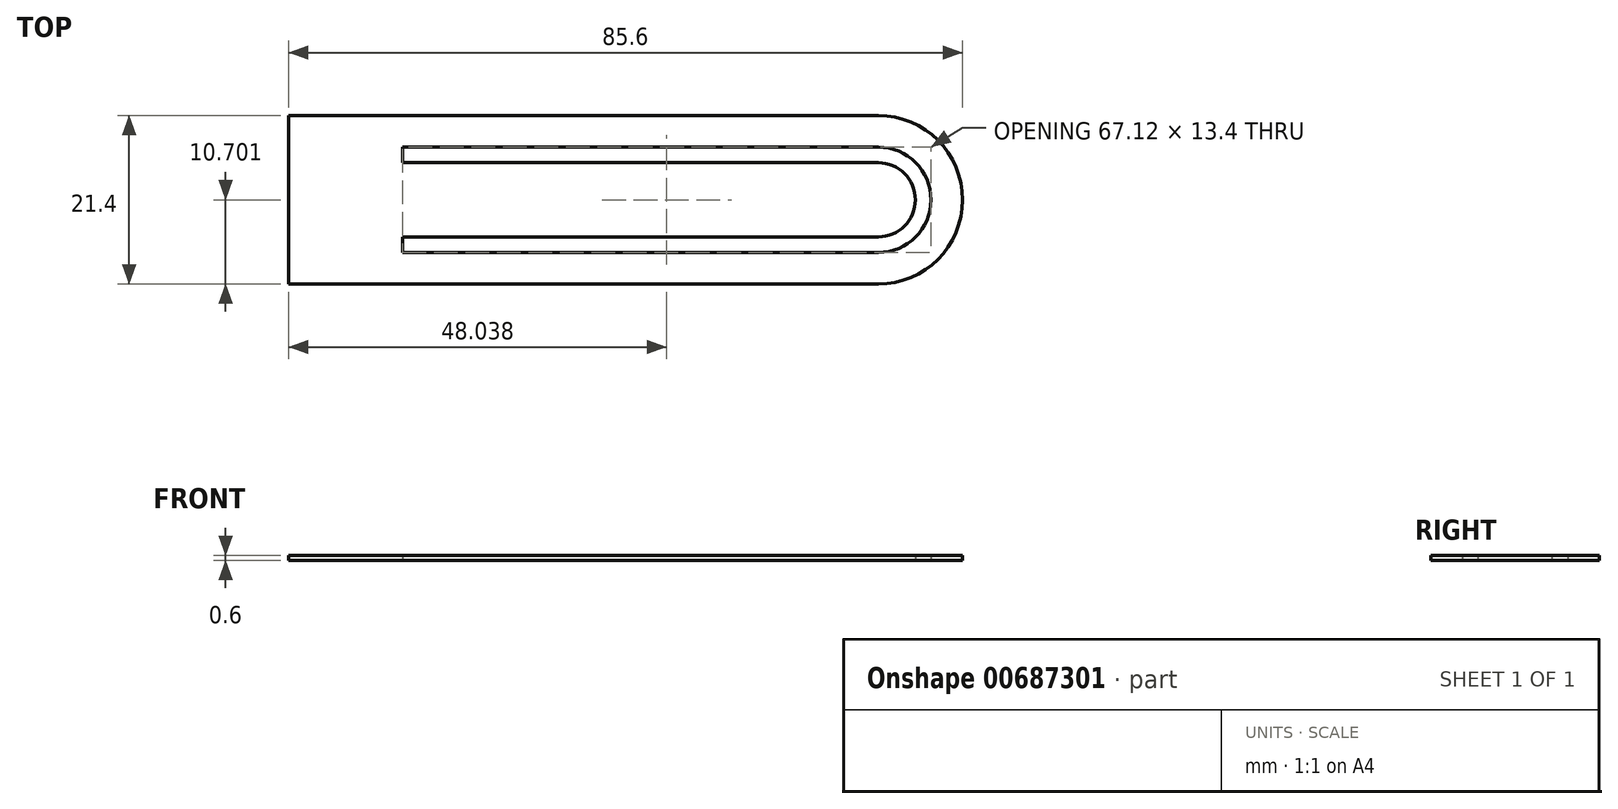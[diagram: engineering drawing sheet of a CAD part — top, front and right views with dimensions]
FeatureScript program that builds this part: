
annotation { "Feature Type Name" : "Feature", "Feature Type Description" : "" }
export const myFeature = defineFeature(function(context is Context, id is Id, definition is map)
    precondition{}
    {
        {
            var Q0;
            Q0=qCreatedBy(makeId("Top.planeOp"),FACE);
            var sketch = newSketch(context, id + "F0", { "sketchPlane" : qUnion([Q0])});
            skLineSegment(sketch, "E0.bottom", {"start": v(32.1, -13.46) * mm, "end": v(-42.8, -13.46) * mm});
            skLineSegment(sketch, "E0.top", {"start": v(32.1, 7.94) * mm, "end": v(-42.8, 7.94) * mm});
            skLineSegment(sketch, "E0.left", {"start": v(42.8, -2.76) * mm, "end": v(42.8, -2.76) * mm});
            skLineSegment(sketch, "E0.right", {"start": v(-42.8, -13.46) * mm, "end": v(-42.8, 7.94) * mm});
            skPoint(sketch, "E0.middle", {"position": v(0, -2.76) * mm});
            skPoint(sketch, "E1.visualSharp", {"position": v(42.8, 7.94) * mm});
            skArc(sketch, "E1.filletArc", {"start": v(42.8, -2.76) * mm, "mid": v(39.67, 4.8) * mm, "end": v(32.1, 7.94) * mm});
            skPoint(sketch, "E2.visualSharp", {"position": v(42.8, -13.46) * mm});
            skArc(sketch, "E2.filletArc", {"start": v(32.1, -13.46) * mm, "mid": v(39.67, -10.32) * mm, "end": v(42.8, -2.76) * mm});
            skLineSegment(sketch, "E3.1", {"start": v(32.1, 3.94) * mm, "end": v(-28.32, 3.94) * mm});
            skLineSegment(sketch, "E3.2", {"start": v(32.1, -9.46) * mm, "end": v(-28.32, -9.46) * mm});
            skArc(sketch, "E3.3", {"start": v(32.1, -9.46) * mm, "mid": v(36.84, -7.5) * mm, "end": v(38.8, -2.76) * mm});
            skArc(sketch, "E3.4", {"start": v(38.8, -2.76) * mm, "mid": v(36.84, 1.98) * mm, "end": v(32.1, 3.94) * mm});
            skLineSegment(sketch, "E4.0", {"start": v(32, 1.94) * mm, "end": v(-28.32, 1.94) * mm});
            skText(sketch, "E5", { "text": "LIBERTO", "fontName": "AllertaStencil-Regular.ttf"});
            skLineSegment(sketch, "E6.0", {"start": v(32.1, -7.46) * mm, "end": v(-28.32, -7.46) * mm});
            skArc(sketch, "E7.0", {"start": v(36.8, -2.76) * mm, "mid": v(35.42, 0.56) * mm, "end": v(32.1, 1.94) * mm});
            skArc(sketch, "E7.1", {"start": v(32.1, -7.46) * mm, "mid": v(35.42, -6.08) * mm, "end": v(36.8, -2.76) * mm});
            skLineSegment(sketch, "E8", {"start": v(-28.32, 3.94) * mm, "end": v(-28.32, 1.94) * mm});
            skLineSegment(sketch, "E9.trimOffspring", {"start": v(-28.32, -7.46) * mm, "end": v(-28.32, -9.46) * mm});
            skLineSegment(sketch, "E10", {"start": v(32, 1.94) * mm, "end": v(32.1, 1.94) * mm});
            const initialGuessF0  = {"E5": [-0.03845, -0.01246, 0, 1, 0.00335]};
            skSetInitialGuess(sketch, initialGuessF0);
            skSolve(sketch);
        }
        {
            var Q0;
            Q0=qCreatedBy(makeId("Top.planeOp"),FACE);
            var sketch = newSketch(context, id + "F1", { "sketchPlane" : qUnion([Q0])});
            skLineSegment(sketch, "E11.bottom", {"start": v(-36.45, -3.76) * mm, "end": v(-34.45, -3.76) * mm});
            skLineSegment(sketch, "E11.top", {"start": v(-36.45, -5.76) * mm, "end": v(-34.45, -5.76) * mm});
            skLineSegment(sketch, "E11.left", {"start": v(-36.45, -3.76) * mm, "end": v(-36.45, -5.76) * mm});
            skLineSegment(sketch, "E11.right", {"start": v(-34.45, -3.76) * mm, "end": v(-34.45, -5.76) * mm});
            skLineSegment(sketch, "E12.bottom", {"start": v(-36.45, 0.24) * mm, "end": v(-34.45, 0.24) * mm});
            skLineSegment(sketch, "E12.top", {"start": v(-36.45, -1.76) * mm, "end": v(-34.45, -1.76) * mm});
            skLineSegment(sketch, "E12.left", {"start": v(-36.45, 0.24) * mm, "end": v(-36.45, -1.76) * mm});
            skLineSegment(sketch, "E12.right", {"start": v(-34.45, 0.24) * mm, "end": v(-34.45, -1.76) * mm});
            skLineSegment(sketch, "E13", {"start": v(-34.45, -1.76) * mm, "end": v(-34.45, -3.76) * mm});
            skLineSegment(sketch, "E14", {"start": v(-34.45, -1.76) * mm, "end": v(-33.45, -1.76) * mm});
            skLineSegment(sketch, "E15", {"start": v(-33.45, -1.76) * mm, "end": v(-33.45, -0.76) * mm});
            skLineSegment(sketch, "E16", {"start": v(-33.45, -0.76) * mm, "end": v(-30.45, -0.76) * mm});
            skLineSegment(sketch, "E17", {"start": v(-30.45, -0.76) * mm, "end": v(-30.45, -1.76) * mm});
            skLineSegment(sketch, "E18", {"start": v(-30.45, -1.76) * mm, "end": v(-31.45, -1.76) * mm});
            skLineSegment(sketch, "E19", {"start": v(-31.45, -1.76) * mm, "end": v(-31.45, -3.76) * mm});
            skLineSegment(sketch, "E20", {"start": v(-31.45, -3.76) * mm, "end": v(-30.45, -3.76) * mm});
            skLineSegment(sketch, "E21", {"start": v(-30.45, -3.76) * mm, "end": v(-30.45, -4.76) * mm});
            skLineSegment(sketch, "E22", {"start": v(-30.45, -4.76) * mm, "end": v(-33.45, -4.76) * mm});
            skLineSegment(sketch, "E23", {"start": v(-33.45, -4.76) * mm, "end": v(-33.45, -3.76) * mm});
            skLineSegment(sketch, "E24", {"start": v(-33.45, -3.76) * mm, "end": v(-34.45, -3.76) * mm});
            skLineSegment(sketch, "E25", {"start": v(-34.41, -3.76) * mm, "end": v(-34.41, -1.76) * mm});
            skSolve(sketch);
        }
        {
            var Q0;
            Q0=makeQuery(id+"F1.imprint","IMPRINT",FACE,{"disambiguationData":[TD([[makeQuery(id+"F1.imprint","IMPRINT",EDGE,{"derivedFrom":sQuery(id+"F1.wireOp",EDGE,"E12.bottom")}),-1.0]])]});
            var Q1;
            Q1=makeQuery(id+"F1.imprint","IMPRINT",FACE,{"disambiguationData":[TD([[makeQuery(id+"F1.imprint","IMPRINT",EDGE,{"derivedFrom":sQuery(id+"F1.wireOp",EDGE,"E11.bottom")}),-1.0]])]});
            extrude(context, id + "F2", {"entities" : qUnion([Q0, Q1]), "depth" : .6 * mm, "offsetDistance" : 25 * mm});
        }
        {
            var Q0;
            Q0=makeQuery(id+"F0.imprint","IMPRINT",FACE,{"disambiguationData":[TD([[makeQuery(id+"F0.imprint","IMPRINT",EDGE,{"derivedFrom":sQuery(id+"F0.wireOp",EDGE,"E0.bottom")}),-1.0]])]});
            extrude(context, id + "F3", {"entities" : qUnion([Q0]), "depth" : .6 * mm, "offsetDistance" : 25 * mm});
        }
        {
            var Q0;
            Q0=makeQuery(id+"F2.opExtrude","SWEPT_BODY",BODY,{"disambiguationData":[OSD([sQuery(id+"F1.wireOp",EDGE,"E11.bottom"),sQuery(id+"F1.wireOp",EDGE,"E11.top"),sQuery(id+"F1.wireOp",EDGE,"E11.left"),sQuery(id+"F1.wireOp",EDGE,"E11.right")])]});
            var Q1;
            Q1=makeQuery(id+"F3.opExtrude","SWEPT_BODY",BODY,{"disambiguationData":[OSD([sQuery(id+"F0.wireOp",EDGE,"E0.bottom"),sQuery(id+"F0.wireOp",EDGE,"E0.top"),sQuery(id+"F0.wireOp",EDGE,"E0.right"),sQuery(id+"F0.wireOp",EDGE,"E1.filletArc"),sQuery(id+"F0.wireOp",EDGE,"E2.filletArc"),sQuery(id+"F0.wireOp",EDGE,"E3.1"),sQuery(id+"F0.wireOp",EDGE,"E3.2"),sQuery(id+"F0.wireOp",EDGE,"E3.3"),sQuery(id+"F0.wireOp",EDGE,"E3.4"),sQuery(id+"F0.wireOp",EDGE,"E4.0"),sQuery(id+"F0.wireOp",EDGE,"E5.sketch_text.stroke-0"),sQuery(id+"F0.wireOp",EDGE,"E5.sketch_text.stroke-1"),sQuery(id+"F0.wireOp",EDGE,"E5.sketch_text.stroke-2"),sQuery(id+"F0.wireOp",EDGE,"E5.sketch_text.stroke-3"),sQuery(id+"F0.wireOp",EDGE,"E5.sketch_text.stroke-4"),sQuery(id+"F0.wireOp",EDGE,"E5.sketch_text.stroke-5"),sQuery(id+"F0.wireOp",EDGE,"E5.sketch_text.stroke-6"),sQuery(id+"F0.wireOp",EDGE,"E5.sketch_text.stroke-7"),sQuery(id+"F0.wireOp",EDGE,"E5.sketch_text.stroke-8"),sQuery(id+"F0.wireOp",EDGE,"E5.sketch_text.stroke-9"),sQuery(id+"F0.wireOp",EDGE,"E5.sketch_text.stroke-10"),sQuery(id+"F0.wireOp",EDGE,"E5.sketch_text.stroke-11"),sQuery(id+"F0.wireOp",EDGE,"E5.sketch_text.stroke-12"),sQuery(id+"F0.wireOp",EDGE,"E5.sketch_text.stroke-13"),sQuery(id+"F0.wireOp",EDGE,"E5.sketch_text.stroke-14"),sQuery(id+"F0.wireOp",EDGE,"E5.sketch_text.stroke-15"),sQuery(id+"F0.wireOp",EDGE,"E5.sketch_text.stroke-16"),sQuery(id+"F0.wireOp",EDGE,"E5.sketch_text.stroke-17"),sQuery(id+"F0.wireOp",EDGE,"E5.sketch_text.stroke-18"),sQuery(id+"F0.wireOp",EDGE,"E5.sketch_text.stroke-19"),sQuery(id+"F0.wireOp",EDGE,"E5.sketch_text.stroke-20"),sQuery(id+"F0.wireOp",EDGE,"E5.sketch_text.stroke-21"),sQuery(id+"F0.wireOp",EDGE,"E5.sketch_text.stroke-22"),sQuery(id+"F0.wireOp",EDGE,"E5.sketch_text.stroke-23"),sQuery(id+"F0.wireOp",EDGE,"E5.sketch_text.stroke-24"),sQuery(id+"F0.wireOp",EDGE,"E5.sketch_text.stroke-25"),sQuery(id+"F0.wireOp",EDGE,"E5.sketch_text.stroke-26"),sQuery(id+"F0.wireOp",EDGE,"E5.sketch_text.stroke-27"),sQuery(id+"F0.wireOp",EDGE,"E5.sketch_text.stroke-28"),sQuery(id+"F0.wireOp",EDGE,"E5.sketch_text.stroke-29"),sQuery(id+"F0.wireOp",EDGE,"E5.sketch_text.stroke-30"),sQuery(id+"F0.wireOp",EDGE,"E5.sketch_text.stroke-31"),sQuery(id+"F0.wireOp",EDGE,"E5.sketch_text.stroke-32"),sQuery(id+"F0.wireOp",EDGE,"E5.sketch_text.stroke-33"),sQuery(id+"F0.wireOp",EDGE,"E5.sketch_text.stroke-34"),sQuery(id+"F0.wireOp",EDGE,"E5.sketch_text.stroke-35"),sQuery(id+"F0.wireOp",EDGE,"E5.sketch_text.stroke-36"),sQuery(id+"F0.wireOp",EDGE,"E5.sketch_text.stroke-37"),sQuery(id+"F0.wireOp",EDGE,"E5.sketch_text.stroke-38"),sQuery(id+"F0.wireOp",EDGE,"E5.sketch_text.stroke-39"),sQuery(id+"F0.wireOp",EDGE,"E5.sketch_text.stroke-40"),sQuery(id+"F0.wireOp",EDGE,"E5.sketch_text.stroke-41"),sQuery(id+"F0.wireOp",EDGE,"E5.sketch_text.stroke-42"),sQuery(id+"F0.wireOp",EDGE,"E5.sketch_text.stroke-43"),sQuery(id+"F0.wireOp",EDGE,"E5.sketch_text.stroke-44"),sQuery(id+"F0.wireOp",EDGE,"E5.sketch_text.stroke-45"),sQuery(id+"F0.wireOp",EDGE,"E5.sketch_text.stroke-46"),sQuery(id+"F0.wireOp",EDGE,"E5.sketch_text.stroke-47"),sQuery(id+"F0.wireOp",EDGE,"E5.sketch_text.stroke-48"),sQuery(id+"F0.wireOp",EDGE,"E5.sketch_text.stroke-49"),sQuery(id+"F0.wireOp",EDGE,"E5.sketch_text.stroke-50"),sQuery(id+"F0.wireOp",EDGE,"E5.sketch_text.stroke-51"),sQuery(id+"F0.wireOp",EDGE,"E5.sketch_text.stroke-52"),sQuery(id+"F0.wireOp",EDGE,"E5.sketch_text.stroke-53"),sQuery(id+"F0.wireOp",EDGE,"E5.sketch_text.stroke-54"),sQuery(id+"F0.wireOp",EDGE,"E5.sketch_text.stroke-55"),sQuery(id+"F0.wireOp",EDGE,"E5.sketch_text.stroke-56"),sQuery(id+"F0.wireOp",EDGE,"E5.sketch_text.stroke-57"),sQuery(id+"F0.wireOp",EDGE,"E5.sketch_text.stroke-58"),sQuery(id+"F0.wireOp",EDGE,"E5.sketch_text.stroke-59"),sQuery(id+"F0.wireOp",EDGE,"E5.sketch_text.stroke-60"),sQuery(id+"F0.wireOp",EDGE,"E5.sketch_text.stroke-61"),sQuery(id+"F0.wireOp",EDGE,"E5.sketch_text.stroke-62"),sQuery(id+"F0.wireOp",EDGE,"E5.sketch_text.stroke-63"),sQuery(id+"F0.wireOp",EDGE,"E5.sketch_text.stroke-64"),sQuery(id+"F0.wireOp",EDGE,"E5.sketch_text.stroke-65"),sQuery(id+"F0.wireOp",EDGE,"E5.sketch_text.stroke-66"),sQuery(id+"F0.wireOp",EDGE,"E5.sketch_text.stroke-67"),sQuery(id+"F0.wireOp",EDGE,"E5.sketch_text.stroke-68"),sQuery(id+"F0.wireOp",EDGE,"E5.sketch_text.stroke-69"),sQuery(id+"F0.wireOp",EDGE,"E5.sketch_text.stroke-70"),sQuery(id+"F0.wireOp",EDGE,"E5.sketch_text.stroke-71"),sQuery(id+"F0.wireOp",EDGE,"E5.sketch_text.stroke-72"),sQuery(id+"F0.wireOp",EDGE,"E5.sketch_text.stroke-73"),sQuery(id+"F0.wireOp",EDGE,"E5.sketch_text.stroke-74"),sQuery(id+"F0.wireOp",EDGE,"E5.sketch_text.stroke-75"),sQuery(id+"F0.wireOp",EDGE,"E5.sketch_text.stroke-76"),sQuery(id+"F0.wireOp",EDGE,"E5.sketch_text.stroke-77"),sQuery(id+"F0.wireOp",EDGE,"E5.sketch_text.stroke-78"),sQuery(id+"F0.wireOp",EDGE,"E5.sketch_text.stroke-79"),sQuery(id+"F0.wireOp",EDGE,"E5.sketch_text.stroke-80"),sQuery(id+"F0.wireOp",EDGE,"E5.sketch_text.stroke-81"),sQuery(id+"F0.wireOp",EDGE,"E5.sketch_text.stroke-82"),sQuery(id+"F0.wireOp",EDGE,"E5.sketch_text.stroke-83"),sQuery(id+"F0.wireOp",EDGE,"E5.sketch_text.stroke-84"),sQuery(id+"F0.wireOp",EDGE,"E5.sketch_text.stroke-85"),sQuery(id+"F0.wireOp",EDGE,"E5.sketch_text.stroke-86"),sQuery(id+"F0.wireOp",EDGE,"E5.sketch_text.stroke-87"),sQuery(id+"F0.wireOp",EDGE,"E5.sketch_text.stroke-88"),sQuery(id+"F0.wireOp",EDGE,"E5.sketch_text.stroke-89"),sQuery(id+"F0.wireOp",EDGE,"E5.sketch_text.stroke-90"),sQuery(id+"F0.wireOp",EDGE,"E5.sketch_text.stroke-91"),sQuery(id+"F0.wireOp",EDGE,"E5.sketch_text.stroke-92"),sQuery(id+"F0.wireOp",EDGE,"E5.sketch_text.stroke-93"),sQuery(id+"F0.wireOp",EDGE,"E5.sketch_text.stroke-94"),sQuery(id+"F0.wireOp",EDGE,"E5.sketch_text.stroke-95"),sQuery(id+"F0.wireOp",EDGE,"E5.sketch_text.stroke-96"),sQuery(id+"F0.wireOp",EDGE,"E5.sketch_text.stroke-97"),sQuery(id+"F0.wireOp",EDGE,"E5.sketch_text.stroke-98"),sQuery(id+"F0.wireOp",EDGE,"E5.sketch_text.stroke-99"),sQuery(id+"F0.wireOp",EDGE,"E5.sketch_text.stroke-100"),sQuery(id+"F0.wireOp",EDGE,"E5.sketch_text.stroke-101"),sQuery(id+"F0.wireOp",EDGE,"E5.sketch_text.stroke-102"),sQuery(id+"F0.wireOp",EDGE,"E5.sketch_text.stroke-103"),sQuery(id+"F0.wireOp",EDGE,"E5.sketch_text.stroke-104"),sQuery(id+"F0.wireOp",EDGE,"E5.sketch_text.stroke-105"),sQuery(id+"F0.wireOp",EDGE,"E5.sketch_text.stroke-106"),sQuery(id+"F0.wireOp",EDGE,"E5.sketch_text.stroke-107"),sQuery(id+"F0.wireOp",EDGE,"E5.sketch_text.stroke-108"),sQuery(id+"F0.wireOp",EDGE,"E5.sketch_text.stroke-109"),sQuery(id+"F0.wireOp",EDGE,"E5.sketch_text.stroke-110"),sQuery(id+"F0.wireOp",EDGE,"E5.sketch_text.stroke-111"),sQuery(id+"F0.wireOp",EDGE,"E5.sketch_text.stroke-112"),sQuery(id+"F0.wireOp",EDGE,"E5.sketch_text.stroke-113"),sQuery(id+"F0.wireOp",EDGE,"E5.sketch_text.stroke-114"),sQuery(id+"F0.wireOp",EDGE,"E5.sketch_text.stroke-115"),sQuery(id+"F0.wireOp",EDGE,"E5.sketch_text.stroke-116"),sQuery(id+"F0.wireOp",EDGE,"E5.sketch_text.stroke-117"),sQuery(id+"F0.wireOp",EDGE,"E5.sketch_text.stroke-118"),sQuery(id+"F0.wireOp",EDGE,"E5.sketch_text.stroke-119"),sQuery(id+"F0.wireOp",EDGE,"E5.sketch_text.stroke-120"),sQuery(id+"F0.wireOp",EDGE,"E5.sketch_text.stroke-121"),sQuery(id+"F0.wireOp",EDGE,"E5.sketch_text.stroke-122"),sQuery(id+"F0.wireOp",EDGE,"E5.sketch_text.stroke-123"),sQuery(id+"F0.wireOp",EDGE,"E5.sketch_text.stroke-124"),sQuery(id+"F0.wireOp",EDGE,"E5.sketch_text.stroke-125"),sQuery(id+"F0.wireOp",EDGE,"E5.sketch_text.stroke-126"),sQuery(id+"F0.wireOp",EDGE,"E5.sketch_text.stroke-127"),sQuery(id+"F0.wireOp",EDGE,"E5.sketch_text.stroke-128"),sQuery(id+"F0.wireOp",EDGE,"E5.sketch_text.stroke-129"),sQuery(id+"F0.wireOp",EDGE,"E5.sketch_text.stroke-130"),sQuery(id+"F0.wireOp",EDGE,"E5.sketch_text.stroke-131"),sQuery(id+"F0.wireOp",EDGE,"E5.sketch_text.stroke-132"),sQuery(id+"F0.wireOp",EDGE,"E5.sketch_text.stroke-133"),sQuery(id+"F0.wireOp",EDGE,"E5.sketch_text.stroke-134"),sQuery(id+"F0.wireOp",EDGE,"E5.sketch_text.stroke-135"),sQuery(id+"F0.wireOp",EDGE,"E5.sketch_text.stroke-136"),sQuery(id+"F0.wireOp",EDGE,"E5.sketch_text.stroke-137"),sQuery(id+"F0.wireOp",EDGE,"E5.sketch_text.stroke-138"),sQuery(id+"F0.wireOp",EDGE,"E5.sketch_text.stroke-139"),sQuery(id+"F0.wireOp",EDGE,"E5.sketch_text.stroke-140"),sQuery(id+"F0.wireOp",EDGE,"E5.sketch_text.stroke-141"),sQuery(id+"F0.wireOp",EDGE,"E5.sketch_text.stroke-142"),sQuery(id+"F0.wireOp",EDGE,"E6.0"),sQuery(id+"F0.wireOp",EDGE,"E7.0"),sQuery(id+"F0.wireOp",EDGE,"E7.1"),sQuery(id+"F0.wireOp",EDGE,"E8"),sQuery(id+"F0.wireOp",EDGE,"E9.trimOffspring"),sQuery(id+"F0.wireOp",EDGE,"E10")])]});
            booleanBodies(context, id + "F4", {"operationType" : BooleanOperationType.SUBTRACTION, "tools" : qUnion([Q0]), "targets" : qUnion([Q1])});
        }
        {
            var Q0;
            Q0=makeQuery(id+"F2.opExtrude","SWEPT_BODY",BODY,{"disambiguationData":[OSD([sQuery(id+"F1.wireOp",EDGE,"E12.bottom"),sQuery(id+"F1.wireOp",EDGE,"E12.top"),sQuery(id+"F1.wireOp",EDGE,"E12.left"),sQuery(id+"F1.wireOp",EDGE,"E12.right")])]});
            var Q1;
            Q1=makeQuery(id+"F3.opExtrude","SWEPT_BODY",BODY,{"disambiguationData":[OSD([sQuery(id+"F0.wireOp",EDGE,"E0.bottom"),sQuery(id+"F0.wireOp",EDGE,"E0.top"),sQuery(id+"F0.wireOp",EDGE,"E0.right"),sQuery(id+"F0.wireOp",EDGE,"E1.filletArc"),sQuery(id+"F0.wireOp",EDGE,"E2.filletArc"),sQuery(id+"F0.wireOp",EDGE,"E3.1"),sQuery(id+"F0.wireOp",EDGE,"E3.2"),sQuery(id+"F0.wireOp",EDGE,"E3.3"),sQuery(id+"F0.wireOp",EDGE,"E3.4"),sQuery(id+"F0.wireOp",EDGE,"E4.0"),sQuery(id+"F0.wireOp",EDGE,"E5.sketch_text.stroke-0"),sQuery(id+"F0.wireOp",EDGE,"E5.sketch_text.stroke-1"),sQuery(id+"F0.wireOp",EDGE,"E5.sketch_text.stroke-2"),sQuery(id+"F0.wireOp",EDGE,"E5.sketch_text.stroke-3"),sQuery(id+"F0.wireOp",EDGE,"E5.sketch_text.stroke-4"),sQuery(id+"F0.wireOp",EDGE,"E5.sketch_text.stroke-5"),sQuery(id+"F0.wireOp",EDGE,"E5.sketch_text.stroke-6"),sQuery(id+"F0.wireOp",EDGE,"E5.sketch_text.stroke-7"),sQuery(id+"F0.wireOp",EDGE,"E5.sketch_text.stroke-8"),sQuery(id+"F0.wireOp",EDGE,"E5.sketch_text.stroke-9"),sQuery(id+"F0.wireOp",EDGE,"E5.sketch_text.stroke-10"),sQuery(id+"F0.wireOp",EDGE,"E5.sketch_text.stroke-11"),sQuery(id+"F0.wireOp",EDGE,"E5.sketch_text.stroke-12"),sQuery(id+"F0.wireOp",EDGE,"E5.sketch_text.stroke-13"),sQuery(id+"F0.wireOp",EDGE,"E5.sketch_text.stroke-14"),sQuery(id+"F0.wireOp",EDGE,"E5.sketch_text.stroke-15"),sQuery(id+"F0.wireOp",EDGE,"E5.sketch_text.stroke-16"),sQuery(id+"F0.wireOp",EDGE,"E5.sketch_text.stroke-17"),sQuery(id+"F0.wireOp",EDGE,"E5.sketch_text.stroke-18"),sQuery(id+"F0.wireOp",EDGE,"E5.sketch_text.stroke-19"),sQuery(id+"F0.wireOp",EDGE,"E5.sketch_text.stroke-20"),sQuery(id+"F0.wireOp",EDGE,"E5.sketch_text.stroke-21"),sQuery(id+"F0.wireOp",EDGE,"E5.sketch_text.stroke-22"),sQuery(id+"F0.wireOp",EDGE,"E5.sketch_text.stroke-23"),sQuery(id+"F0.wireOp",EDGE,"E5.sketch_text.stroke-24"),sQuery(id+"F0.wireOp",EDGE,"E5.sketch_text.stroke-25"),sQuery(id+"F0.wireOp",EDGE,"E5.sketch_text.stroke-26"),sQuery(id+"F0.wireOp",EDGE,"E5.sketch_text.stroke-27"),sQuery(id+"F0.wireOp",EDGE,"E5.sketch_text.stroke-28"),sQuery(id+"F0.wireOp",EDGE,"E5.sketch_text.stroke-29"),sQuery(id+"F0.wireOp",EDGE,"E5.sketch_text.stroke-30"),sQuery(id+"F0.wireOp",EDGE,"E5.sketch_text.stroke-31"),sQuery(id+"F0.wireOp",EDGE,"E5.sketch_text.stroke-32"),sQuery(id+"F0.wireOp",EDGE,"E5.sketch_text.stroke-33"),sQuery(id+"F0.wireOp",EDGE,"E5.sketch_text.stroke-34"),sQuery(id+"F0.wireOp",EDGE,"E5.sketch_text.stroke-35"),sQuery(id+"F0.wireOp",EDGE,"E5.sketch_text.stroke-36"),sQuery(id+"F0.wireOp",EDGE,"E5.sketch_text.stroke-37"),sQuery(id+"F0.wireOp",EDGE,"E5.sketch_text.stroke-38"),sQuery(id+"F0.wireOp",EDGE,"E5.sketch_text.stroke-39"),sQuery(id+"F0.wireOp",EDGE,"E5.sketch_text.stroke-40"),sQuery(id+"F0.wireOp",EDGE,"E5.sketch_text.stroke-41"),sQuery(id+"F0.wireOp",EDGE,"E5.sketch_text.stroke-42"),sQuery(id+"F0.wireOp",EDGE,"E5.sketch_text.stroke-43"),sQuery(id+"F0.wireOp",EDGE,"E5.sketch_text.stroke-44"),sQuery(id+"F0.wireOp",EDGE,"E5.sketch_text.stroke-45"),sQuery(id+"F0.wireOp",EDGE,"E5.sketch_text.stroke-46"),sQuery(id+"F0.wireOp",EDGE,"E5.sketch_text.stroke-47"),sQuery(id+"F0.wireOp",EDGE,"E5.sketch_text.stroke-48"),sQuery(id+"F0.wireOp",EDGE,"E5.sketch_text.stroke-49"),sQuery(id+"F0.wireOp",EDGE,"E5.sketch_text.stroke-50"),sQuery(id+"F0.wireOp",EDGE,"E5.sketch_text.stroke-51"),sQuery(id+"F0.wireOp",EDGE,"E5.sketch_text.stroke-52"),sQuery(id+"F0.wireOp",EDGE,"E5.sketch_text.stroke-53"),sQuery(id+"F0.wireOp",EDGE,"E5.sketch_text.stroke-54"),sQuery(id+"F0.wireOp",EDGE,"E5.sketch_text.stroke-55"),sQuery(id+"F0.wireOp",EDGE,"E5.sketch_text.stroke-56"),sQuery(id+"F0.wireOp",EDGE,"E5.sketch_text.stroke-57"),sQuery(id+"F0.wireOp",EDGE,"E5.sketch_text.stroke-58"),sQuery(id+"F0.wireOp",EDGE,"E5.sketch_text.stroke-59"),sQuery(id+"F0.wireOp",EDGE,"E5.sketch_text.stroke-60"),sQuery(id+"F0.wireOp",EDGE,"E5.sketch_text.stroke-61"),sQuery(id+"F0.wireOp",EDGE,"E5.sketch_text.stroke-62"),sQuery(id+"F0.wireOp",EDGE,"E5.sketch_text.stroke-63"),sQuery(id+"F0.wireOp",EDGE,"E5.sketch_text.stroke-64"),sQuery(id+"F0.wireOp",EDGE,"E5.sketch_text.stroke-65"),sQuery(id+"F0.wireOp",EDGE,"E5.sketch_text.stroke-66"),sQuery(id+"F0.wireOp",EDGE,"E5.sketch_text.stroke-67"),sQuery(id+"F0.wireOp",EDGE,"E5.sketch_text.stroke-68"),sQuery(id+"F0.wireOp",EDGE,"E5.sketch_text.stroke-69"),sQuery(id+"F0.wireOp",EDGE,"E5.sketch_text.stroke-70"),sQuery(id+"F0.wireOp",EDGE,"E5.sketch_text.stroke-71"),sQuery(id+"F0.wireOp",EDGE,"E5.sketch_text.stroke-72"),sQuery(id+"F0.wireOp",EDGE,"E5.sketch_text.stroke-73"),sQuery(id+"F0.wireOp",EDGE,"E5.sketch_text.stroke-74"),sQuery(id+"F0.wireOp",EDGE,"E5.sketch_text.stroke-75"),sQuery(id+"F0.wireOp",EDGE,"E5.sketch_text.stroke-76"),sQuery(id+"F0.wireOp",EDGE,"E5.sketch_text.stroke-77"),sQuery(id+"F0.wireOp",EDGE,"E5.sketch_text.stroke-78"),sQuery(id+"F0.wireOp",EDGE,"E5.sketch_text.stroke-79"),sQuery(id+"F0.wireOp",EDGE,"E5.sketch_text.stroke-80"),sQuery(id+"F0.wireOp",EDGE,"E5.sketch_text.stroke-81"),sQuery(id+"F0.wireOp",EDGE,"E5.sketch_text.stroke-82"),sQuery(id+"F0.wireOp",EDGE,"E5.sketch_text.stroke-83"),sQuery(id+"F0.wireOp",EDGE,"E5.sketch_text.stroke-84"),sQuery(id+"F0.wireOp",EDGE,"E5.sketch_text.stroke-85"),sQuery(id+"F0.wireOp",EDGE,"E5.sketch_text.stroke-86"),sQuery(id+"F0.wireOp",EDGE,"E5.sketch_text.stroke-87"),sQuery(id+"F0.wireOp",EDGE,"E5.sketch_text.stroke-88"),sQuery(id+"F0.wireOp",EDGE,"E5.sketch_text.stroke-89"),sQuery(id+"F0.wireOp",EDGE,"E5.sketch_text.stroke-90"),sQuery(id+"F0.wireOp",EDGE,"E5.sketch_text.stroke-91"),sQuery(id+"F0.wireOp",EDGE,"E5.sketch_text.stroke-92"),sQuery(id+"F0.wireOp",EDGE,"E5.sketch_text.stroke-93"),sQuery(id+"F0.wireOp",EDGE,"E5.sketch_text.stroke-94"),sQuery(id+"F0.wireOp",EDGE,"E5.sketch_text.stroke-95"),sQuery(id+"F0.wireOp",EDGE,"E5.sketch_text.stroke-96"),sQuery(id+"F0.wireOp",EDGE,"E5.sketch_text.stroke-97"),sQuery(id+"F0.wireOp",EDGE,"E5.sketch_text.stroke-98"),sQuery(id+"F0.wireOp",EDGE,"E5.sketch_text.stroke-99"),sQuery(id+"F0.wireOp",EDGE,"E5.sketch_text.stroke-100"),sQuery(id+"F0.wireOp",EDGE,"E5.sketch_text.stroke-101"),sQuery(id+"F0.wireOp",EDGE,"E5.sketch_text.stroke-102"),sQuery(id+"F0.wireOp",EDGE,"E5.sketch_text.stroke-103"),sQuery(id+"F0.wireOp",EDGE,"E5.sketch_text.stroke-104"),sQuery(id+"F0.wireOp",EDGE,"E5.sketch_text.stroke-105"),sQuery(id+"F0.wireOp",EDGE,"E5.sketch_text.stroke-106"),sQuery(id+"F0.wireOp",EDGE,"E5.sketch_text.stroke-107"),sQuery(id+"F0.wireOp",EDGE,"E5.sketch_text.stroke-108"),sQuery(id+"F0.wireOp",EDGE,"E5.sketch_text.stroke-109"),sQuery(id+"F0.wireOp",EDGE,"E5.sketch_text.stroke-110"),sQuery(id+"F0.wireOp",EDGE,"E5.sketch_text.stroke-111"),sQuery(id+"F0.wireOp",EDGE,"E5.sketch_text.stroke-112"),sQuery(id+"F0.wireOp",EDGE,"E5.sketch_text.stroke-113"),sQuery(id+"F0.wireOp",EDGE,"E5.sketch_text.stroke-114"),sQuery(id+"F0.wireOp",EDGE,"E5.sketch_text.stroke-115"),sQuery(id+"F0.wireOp",EDGE,"E5.sketch_text.stroke-116"),sQuery(id+"F0.wireOp",EDGE,"E5.sketch_text.stroke-117"),sQuery(id+"F0.wireOp",EDGE,"E5.sketch_text.stroke-118"),sQuery(id+"F0.wireOp",EDGE,"E5.sketch_text.stroke-119"),sQuery(id+"F0.wireOp",EDGE,"E5.sketch_text.stroke-120"),sQuery(id+"F0.wireOp",EDGE,"E5.sketch_text.stroke-121"),sQuery(id+"F0.wireOp",EDGE,"E5.sketch_text.stroke-122"),sQuery(id+"F0.wireOp",EDGE,"E5.sketch_text.stroke-123"),sQuery(id+"F0.wireOp",EDGE,"E5.sketch_text.stroke-124"),sQuery(id+"F0.wireOp",EDGE,"E5.sketch_text.stroke-125"),sQuery(id+"F0.wireOp",EDGE,"E5.sketch_text.stroke-126"),sQuery(id+"F0.wireOp",EDGE,"E5.sketch_text.stroke-127"),sQuery(id+"F0.wireOp",EDGE,"E5.sketch_text.stroke-128"),sQuery(id+"F0.wireOp",EDGE,"E5.sketch_text.stroke-129"),sQuery(id+"F0.wireOp",EDGE,"E5.sketch_text.stroke-130"),sQuery(id+"F0.wireOp",EDGE,"E5.sketch_text.stroke-131"),sQuery(id+"F0.wireOp",EDGE,"E5.sketch_text.stroke-132"),sQuery(id+"F0.wireOp",EDGE,"E5.sketch_text.stroke-133"),sQuery(id+"F0.wireOp",EDGE,"E5.sketch_text.stroke-134"),sQuery(id+"F0.wireOp",EDGE,"E5.sketch_text.stroke-135"),sQuery(id+"F0.wireOp",EDGE,"E5.sketch_text.stroke-136"),sQuery(id+"F0.wireOp",EDGE,"E5.sketch_text.stroke-137"),sQuery(id+"F0.wireOp",EDGE,"E5.sketch_text.stroke-138"),sQuery(id+"F0.wireOp",EDGE,"E5.sketch_text.stroke-139"),sQuery(id+"F0.wireOp",EDGE,"E5.sketch_text.stroke-140"),sQuery(id+"F0.wireOp",EDGE,"E5.sketch_text.stroke-141"),sQuery(id+"F0.wireOp",EDGE,"E5.sketch_text.stroke-142"),sQuery(id+"F0.wireOp",EDGE,"E6.0"),sQuery(id+"F0.wireOp",EDGE,"E7.0"),sQuery(id+"F0.wireOp",EDGE,"E7.1"),sQuery(id+"F0.wireOp",EDGE,"E8"),sQuery(id+"F0.wireOp",EDGE,"E9.trimOffspring"),sQuery(id+"F0.wireOp",EDGE,"E10")])]});
            booleanBodies(context, id + "F5", {"operationType" : BooleanOperationType.SUBTRACTION, "tools" : qUnion([Q0]), "targets" : qUnion([Q1])});
        }
        {
            var Q0;
            {var subQ1=sQuery(id+"F1.wireOp",EDGE,"E15");Q0=makeQuery(id+"F1.imprint","IMPRINT",FACE,{"disambiguationData":[TD([[makeQuery(id+"F1.imprint","IMPRINT",EDGE,{"derivedFrom":subQ1}),-1.0]])]});}
            extrude(context, id + "F6", {"entities" : qUnion([Q0]), "depth" : .6 * mm, "offsetDistance" : 25 * mm});
        }
        {
            var Q0;
            Q0=makeQuery(id+"F6.opExtrude","SWEPT_BODY",BODY,{"disambiguationData":[OSD([sQuery(id+"F1.wireOp",EDGE,"E14"),sQuery(id+"F1.wireOp",EDGE,"E15"),sQuery(id+"F1.wireOp",EDGE,"E16"),sQuery(id+"F1.wireOp",EDGE,"E17"),sQuery(id+"F1.wireOp",EDGE,"E18"),sQuery(id+"F1.wireOp",EDGE,"E19"),sQuery(id+"F1.wireOp",EDGE,"E20"),sQuery(id+"F1.wireOp",EDGE,"E21"),sQuery(id+"F1.wireOp",EDGE,"E22"),sQuery(id+"F1.wireOp",EDGE,"E23"),sQuery(id+"F1.wireOp",EDGE,"E24"),sQuery(id+"F1.wireOp",EDGE,"E25")])]});
            var Q1;
            Q1=makeQuery(id+"F3.opExtrude","SWEPT_BODY",BODY,{"disambiguationData":[OSD([sQuery(id+"F0.wireOp",EDGE,"E0.bottom"),sQuery(id+"F0.wireOp",EDGE,"E0.top"),sQuery(id+"F0.wireOp",EDGE,"E0.right"),sQuery(id+"F0.wireOp",EDGE,"E1.filletArc"),sQuery(id+"F0.wireOp",EDGE,"E2.filletArc"),sQuery(id+"F0.wireOp",EDGE,"E3.1"),sQuery(id+"F0.wireOp",EDGE,"E3.2"),sQuery(id+"F0.wireOp",EDGE,"E3.3"),sQuery(id+"F0.wireOp",EDGE,"E3.4"),sQuery(id+"F0.wireOp",EDGE,"E4.0"),sQuery(id+"F0.wireOp",EDGE,"E5.sketch_text.stroke-0"),sQuery(id+"F0.wireOp",EDGE,"E5.sketch_text.stroke-1"),sQuery(id+"F0.wireOp",EDGE,"E5.sketch_text.stroke-2"),sQuery(id+"F0.wireOp",EDGE,"E5.sketch_text.stroke-3"),sQuery(id+"F0.wireOp",EDGE,"E5.sketch_text.stroke-4"),sQuery(id+"F0.wireOp",EDGE,"E5.sketch_text.stroke-5"),sQuery(id+"F0.wireOp",EDGE,"E5.sketch_text.stroke-6"),sQuery(id+"F0.wireOp",EDGE,"E5.sketch_text.stroke-7"),sQuery(id+"F0.wireOp",EDGE,"E5.sketch_text.stroke-8"),sQuery(id+"F0.wireOp",EDGE,"E5.sketch_text.stroke-9"),sQuery(id+"F0.wireOp",EDGE,"E5.sketch_text.stroke-10"),sQuery(id+"F0.wireOp",EDGE,"E5.sketch_text.stroke-11"),sQuery(id+"F0.wireOp",EDGE,"E5.sketch_text.stroke-12"),sQuery(id+"F0.wireOp",EDGE,"E5.sketch_text.stroke-13"),sQuery(id+"F0.wireOp",EDGE,"E5.sketch_text.stroke-14"),sQuery(id+"F0.wireOp",EDGE,"E5.sketch_text.stroke-15"),sQuery(id+"F0.wireOp",EDGE,"E5.sketch_text.stroke-16"),sQuery(id+"F0.wireOp",EDGE,"E5.sketch_text.stroke-17"),sQuery(id+"F0.wireOp",EDGE,"E5.sketch_text.stroke-18"),sQuery(id+"F0.wireOp",EDGE,"E5.sketch_text.stroke-19"),sQuery(id+"F0.wireOp",EDGE,"E5.sketch_text.stroke-20"),sQuery(id+"F0.wireOp",EDGE,"E5.sketch_text.stroke-21"),sQuery(id+"F0.wireOp",EDGE,"E5.sketch_text.stroke-22"),sQuery(id+"F0.wireOp",EDGE,"E5.sketch_text.stroke-23"),sQuery(id+"F0.wireOp",EDGE,"E5.sketch_text.stroke-24"),sQuery(id+"F0.wireOp",EDGE,"E5.sketch_text.stroke-25"),sQuery(id+"F0.wireOp",EDGE,"E5.sketch_text.stroke-26"),sQuery(id+"F0.wireOp",EDGE,"E5.sketch_text.stroke-27"),sQuery(id+"F0.wireOp",EDGE,"E5.sketch_text.stroke-28"),sQuery(id+"F0.wireOp",EDGE,"E5.sketch_text.stroke-29"),sQuery(id+"F0.wireOp",EDGE,"E5.sketch_text.stroke-30"),sQuery(id+"F0.wireOp",EDGE,"E5.sketch_text.stroke-31"),sQuery(id+"F0.wireOp",EDGE,"E5.sketch_text.stroke-32"),sQuery(id+"F0.wireOp",EDGE,"E5.sketch_text.stroke-33"),sQuery(id+"F0.wireOp",EDGE,"E5.sketch_text.stroke-34"),sQuery(id+"F0.wireOp",EDGE,"E5.sketch_text.stroke-35"),sQuery(id+"F0.wireOp",EDGE,"E5.sketch_text.stroke-36"),sQuery(id+"F0.wireOp",EDGE,"E5.sketch_text.stroke-37"),sQuery(id+"F0.wireOp",EDGE,"E5.sketch_text.stroke-38"),sQuery(id+"F0.wireOp",EDGE,"E5.sketch_text.stroke-39"),sQuery(id+"F0.wireOp",EDGE,"E5.sketch_text.stroke-40"),sQuery(id+"F0.wireOp",EDGE,"E5.sketch_text.stroke-41"),sQuery(id+"F0.wireOp",EDGE,"E5.sketch_text.stroke-42"),sQuery(id+"F0.wireOp",EDGE,"E5.sketch_text.stroke-43"),sQuery(id+"F0.wireOp",EDGE,"E5.sketch_text.stroke-44"),sQuery(id+"F0.wireOp",EDGE,"E5.sketch_text.stroke-45"),sQuery(id+"F0.wireOp",EDGE,"E5.sketch_text.stroke-46"),sQuery(id+"F0.wireOp",EDGE,"E5.sketch_text.stroke-47"),sQuery(id+"F0.wireOp",EDGE,"E5.sketch_text.stroke-48"),sQuery(id+"F0.wireOp",EDGE,"E5.sketch_text.stroke-49"),sQuery(id+"F0.wireOp",EDGE,"E5.sketch_text.stroke-50"),sQuery(id+"F0.wireOp",EDGE,"E5.sketch_text.stroke-51"),sQuery(id+"F0.wireOp",EDGE,"E5.sketch_text.stroke-52"),sQuery(id+"F0.wireOp",EDGE,"E5.sketch_text.stroke-53"),sQuery(id+"F0.wireOp",EDGE,"E5.sketch_text.stroke-54"),sQuery(id+"F0.wireOp",EDGE,"E5.sketch_text.stroke-55"),sQuery(id+"F0.wireOp",EDGE,"E5.sketch_text.stroke-56"),sQuery(id+"F0.wireOp",EDGE,"E5.sketch_text.stroke-57"),sQuery(id+"F0.wireOp",EDGE,"E5.sketch_text.stroke-58"),sQuery(id+"F0.wireOp",EDGE,"E5.sketch_text.stroke-59"),sQuery(id+"F0.wireOp",EDGE,"E5.sketch_text.stroke-60"),sQuery(id+"F0.wireOp",EDGE,"E5.sketch_text.stroke-61"),sQuery(id+"F0.wireOp",EDGE,"E5.sketch_text.stroke-62"),sQuery(id+"F0.wireOp",EDGE,"E5.sketch_text.stroke-63"),sQuery(id+"F0.wireOp",EDGE,"E5.sketch_text.stroke-64"),sQuery(id+"F0.wireOp",EDGE,"E5.sketch_text.stroke-65"),sQuery(id+"F0.wireOp",EDGE,"E5.sketch_text.stroke-66"),sQuery(id+"F0.wireOp",EDGE,"E5.sketch_text.stroke-67"),sQuery(id+"F0.wireOp",EDGE,"E5.sketch_text.stroke-68"),sQuery(id+"F0.wireOp",EDGE,"E5.sketch_text.stroke-69"),sQuery(id+"F0.wireOp",EDGE,"E5.sketch_text.stroke-70"),sQuery(id+"F0.wireOp",EDGE,"E5.sketch_text.stroke-71"),sQuery(id+"F0.wireOp",EDGE,"E5.sketch_text.stroke-72"),sQuery(id+"F0.wireOp",EDGE,"E5.sketch_text.stroke-73"),sQuery(id+"F0.wireOp",EDGE,"E5.sketch_text.stroke-74"),sQuery(id+"F0.wireOp",EDGE,"E5.sketch_text.stroke-75"),sQuery(id+"F0.wireOp",EDGE,"E5.sketch_text.stroke-76"),sQuery(id+"F0.wireOp",EDGE,"E5.sketch_text.stroke-77"),sQuery(id+"F0.wireOp",EDGE,"E5.sketch_text.stroke-78"),sQuery(id+"F0.wireOp",EDGE,"E5.sketch_text.stroke-79"),sQuery(id+"F0.wireOp",EDGE,"E5.sketch_text.stroke-80"),sQuery(id+"F0.wireOp",EDGE,"E5.sketch_text.stroke-81"),sQuery(id+"F0.wireOp",EDGE,"E5.sketch_text.stroke-82"),sQuery(id+"F0.wireOp",EDGE,"E5.sketch_text.stroke-83"),sQuery(id+"F0.wireOp",EDGE,"E5.sketch_text.stroke-84"),sQuery(id+"F0.wireOp",EDGE,"E5.sketch_text.stroke-85"),sQuery(id+"F0.wireOp",EDGE,"E5.sketch_text.stroke-86"),sQuery(id+"F0.wireOp",EDGE,"E5.sketch_text.stroke-87"),sQuery(id+"F0.wireOp",EDGE,"E5.sketch_text.stroke-88"),sQuery(id+"F0.wireOp",EDGE,"E5.sketch_text.stroke-89"),sQuery(id+"F0.wireOp",EDGE,"E5.sketch_text.stroke-90"),sQuery(id+"F0.wireOp",EDGE,"E5.sketch_text.stroke-91"),sQuery(id+"F0.wireOp",EDGE,"E5.sketch_text.stroke-92"),sQuery(id+"F0.wireOp",EDGE,"E5.sketch_text.stroke-93"),sQuery(id+"F0.wireOp",EDGE,"E5.sketch_text.stroke-94"),sQuery(id+"F0.wireOp",EDGE,"E5.sketch_text.stroke-95"),sQuery(id+"F0.wireOp",EDGE,"E5.sketch_text.stroke-96"),sQuery(id+"F0.wireOp",EDGE,"E5.sketch_text.stroke-97"),sQuery(id+"F0.wireOp",EDGE,"E5.sketch_text.stroke-98"),sQuery(id+"F0.wireOp",EDGE,"E5.sketch_text.stroke-99"),sQuery(id+"F0.wireOp",EDGE,"E5.sketch_text.stroke-100"),sQuery(id+"F0.wireOp",EDGE,"E5.sketch_text.stroke-101"),sQuery(id+"F0.wireOp",EDGE,"E5.sketch_text.stroke-102"),sQuery(id+"F0.wireOp",EDGE,"E5.sketch_text.stroke-103"),sQuery(id+"F0.wireOp",EDGE,"E5.sketch_text.stroke-104"),sQuery(id+"F0.wireOp",EDGE,"E5.sketch_text.stroke-105"),sQuery(id+"F0.wireOp",EDGE,"E5.sketch_text.stroke-106"),sQuery(id+"F0.wireOp",EDGE,"E5.sketch_text.stroke-107"),sQuery(id+"F0.wireOp",EDGE,"E5.sketch_text.stroke-108"),sQuery(id+"F0.wireOp",EDGE,"E5.sketch_text.stroke-109"),sQuery(id+"F0.wireOp",EDGE,"E5.sketch_text.stroke-110"),sQuery(id+"F0.wireOp",EDGE,"E5.sketch_text.stroke-111"),sQuery(id+"F0.wireOp",EDGE,"E5.sketch_text.stroke-112"),sQuery(id+"F0.wireOp",EDGE,"E5.sketch_text.stroke-113"),sQuery(id+"F0.wireOp",EDGE,"E5.sketch_text.stroke-114"),sQuery(id+"F0.wireOp",EDGE,"E5.sketch_text.stroke-115"),sQuery(id+"F0.wireOp",EDGE,"E5.sketch_text.stroke-116"),sQuery(id+"F0.wireOp",EDGE,"E5.sketch_text.stroke-117"),sQuery(id+"F0.wireOp",EDGE,"E5.sketch_text.stroke-118"),sQuery(id+"F0.wireOp",EDGE,"E5.sketch_text.stroke-119"),sQuery(id+"F0.wireOp",EDGE,"E5.sketch_text.stroke-120"),sQuery(id+"F0.wireOp",EDGE,"E5.sketch_text.stroke-121"),sQuery(id+"F0.wireOp",EDGE,"E5.sketch_text.stroke-122"),sQuery(id+"F0.wireOp",EDGE,"E5.sketch_text.stroke-123"),sQuery(id+"F0.wireOp",EDGE,"E5.sketch_text.stroke-124"),sQuery(id+"F0.wireOp",EDGE,"E5.sketch_text.stroke-125"),sQuery(id+"F0.wireOp",EDGE,"E5.sketch_text.stroke-126"),sQuery(id+"F0.wireOp",EDGE,"E5.sketch_text.stroke-127"),sQuery(id+"F0.wireOp",EDGE,"E5.sketch_text.stroke-128"),sQuery(id+"F0.wireOp",EDGE,"E5.sketch_text.stroke-129"),sQuery(id+"F0.wireOp",EDGE,"E5.sketch_text.stroke-130"),sQuery(id+"F0.wireOp",EDGE,"E5.sketch_text.stroke-131"),sQuery(id+"F0.wireOp",EDGE,"E5.sketch_text.stroke-132"),sQuery(id+"F0.wireOp",EDGE,"E5.sketch_text.stroke-133"),sQuery(id+"F0.wireOp",EDGE,"E5.sketch_text.stroke-134"),sQuery(id+"F0.wireOp",EDGE,"E5.sketch_text.stroke-135"),sQuery(id+"F0.wireOp",EDGE,"E5.sketch_text.stroke-136"),sQuery(id+"F0.wireOp",EDGE,"E5.sketch_text.stroke-137"),sQuery(id+"F0.wireOp",EDGE,"E5.sketch_text.stroke-138"),sQuery(id+"F0.wireOp",EDGE,"E5.sketch_text.stroke-139"),sQuery(id+"F0.wireOp",EDGE,"E5.sketch_text.stroke-140"),sQuery(id+"F0.wireOp",EDGE,"E5.sketch_text.stroke-141"),sQuery(id+"F0.wireOp",EDGE,"E5.sketch_text.stroke-142"),sQuery(id+"F0.wireOp",EDGE,"E6.0"),sQuery(id+"F0.wireOp",EDGE,"E7.0"),sQuery(id+"F0.wireOp",EDGE,"E7.1"),sQuery(id+"F0.wireOp",EDGE,"E8"),sQuery(id+"F0.wireOp",EDGE,"E9.trimOffspring"),sQuery(id+"F0.wireOp",EDGE,"E10")])]});
            booleanBodies(context, id + "F7", {"operationType" : BooleanOperationType.SUBTRACTION, "tools" : qUnion([Q0]), "targets" : qUnion([Q1])});
        }
        {
            var Q0;
            Q0=makeQuery(id+"F3.opExtrude","SWEPT_BODY",BODY,{"disambiguationData":[OSD([sQuery(id+"F0.wireOp",EDGE,"E0.bottom"),sQuery(id+"F0.wireOp",EDGE,"E0.top"),sQuery(id+"F0.wireOp",EDGE,"E0.right"),sQuery(id+"F0.wireOp",EDGE,"E1.filletArc"),sQuery(id+"F0.wireOp",EDGE,"E2.filletArc"),sQuery(id+"F0.wireOp",EDGE,"E3.1"),sQuery(id+"F0.wireOp",EDGE,"E3.2"),sQuery(id+"F0.wireOp",EDGE,"E3.3"),sQuery(id+"F0.wireOp",EDGE,"E3.4"),sQuery(id+"F0.wireOp",EDGE,"E4.0"),sQuery(id+"F0.wireOp",EDGE,"E5.sketch_text.stroke-0"),sQuery(id+"F0.wireOp",EDGE,"E5.sketch_text.stroke-1"),sQuery(id+"F0.wireOp",EDGE,"E5.sketch_text.stroke-2"),sQuery(id+"F0.wireOp",EDGE,"E5.sketch_text.stroke-3"),sQuery(id+"F0.wireOp",EDGE,"E5.sketch_text.stroke-4"),sQuery(id+"F0.wireOp",EDGE,"E5.sketch_text.stroke-5"),sQuery(id+"F0.wireOp",EDGE,"E5.sketch_text.stroke-6"),sQuery(id+"F0.wireOp",EDGE,"E5.sketch_text.stroke-7"),sQuery(id+"F0.wireOp",EDGE,"E5.sketch_text.stroke-8"),sQuery(id+"F0.wireOp",EDGE,"E5.sketch_text.stroke-9"),sQuery(id+"F0.wireOp",EDGE,"E5.sketch_text.stroke-10"),sQuery(id+"F0.wireOp",EDGE,"E5.sketch_text.stroke-11"),sQuery(id+"F0.wireOp",EDGE,"E5.sketch_text.stroke-12"),sQuery(id+"F0.wireOp",EDGE,"E5.sketch_text.stroke-13"),sQuery(id+"F0.wireOp",EDGE,"E5.sketch_text.stroke-14"),sQuery(id+"F0.wireOp",EDGE,"E5.sketch_text.stroke-15"),sQuery(id+"F0.wireOp",EDGE,"E5.sketch_text.stroke-16"),sQuery(id+"F0.wireOp",EDGE,"E5.sketch_text.stroke-17"),sQuery(id+"F0.wireOp",EDGE,"E5.sketch_text.stroke-18"),sQuery(id+"F0.wireOp",EDGE,"E5.sketch_text.stroke-19"),sQuery(id+"F0.wireOp",EDGE,"E5.sketch_text.stroke-20"),sQuery(id+"F0.wireOp",EDGE,"E5.sketch_text.stroke-21"),sQuery(id+"F0.wireOp",EDGE,"E5.sketch_text.stroke-22"),sQuery(id+"F0.wireOp",EDGE,"E5.sketch_text.stroke-23"),sQuery(id+"F0.wireOp",EDGE,"E5.sketch_text.stroke-24"),sQuery(id+"F0.wireOp",EDGE,"E5.sketch_text.stroke-25"),sQuery(id+"F0.wireOp",EDGE,"E5.sketch_text.stroke-26"),sQuery(id+"F0.wireOp",EDGE,"E5.sketch_text.stroke-27"),sQuery(id+"F0.wireOp",EDGE,"E5.sketch_text.stroke-28"),sQuery(id+"F0.wireOp",EDGE,"E5.sketch_text.stroke-29"),sQuery(id+"F0.wireOp",EDGE,"E5.sketch_text.stroke-30"),sQuery(id+"F0.wireOp",EDGE,"E5.sketch_text.stroke-31"),sQuery(id+"F0.wireOp",EDGE,"E5.sketch_text.stroke-32"),sQuery(id+"F0.wireOp",EDGE,"E5.sketch_text.stroke-33"),sQuery(id+"F0.wireOp",EDGE,"E5.sketch_text.stroke-34"),sQuery(id+"F0.wireOp",EDGE,"E5.sketch_text.stroke-35"),sQuery(id+"F0.wireOp",EDGE,"E5.sketch_text.stroke-36"),sQuery(id+"F0.wireOp",EDGE,"E5.sketch_text.stroke-37"),sQuery(id+"F0.wireOp",EDGE,"E5.sketch_text.stroke-38"),sQuery(id+"F0.wireOp",EDGE,"E5.sketch_text.stroke-39"),sQuery(id+"F0.wireOp",EDGE,"E5.sketch_text.stroke-40"),sQuery(id+"F0.wireOp",EDGE,"E5.sketch_text.stroke-41"),sQuery(id+"F0.wireOp",EDGE,"E5.sketch_text.stroke-42"),sQuery(id+"F0.wireOp",EDGE,"E5.sketch_text.stroke-43"),sQuery(id+"F0.wireOp",EDGE,"E5.sketch_text.stroke-44"),sQuery(id+"F0.wireOp",EDGE,"E5.sketch_text.stroke-45"),sQuery(id+"F0.wireOp",EDGE,"E5.sketch_text.stroke-46"),sQuery(id+"F0.wireOp",EDGE,"E5.sketch_text.stroke-47"),sQuery(id+"F0.wireOp",EDGE,"E5.sketch_text.stroke-48"),sQuery(id+"F0.wireOp",EDGE,"E5.sketch_text.stroke-49"),sQuery(id+"F0.wireOp",EDGE,"E5.sketch_text.stroke-50"),sQuery(id+"F0.wireOp",EDGE,"E5.sketch_text.stroke-51"),sQuery(id+"F0.wireOp",EDGE,"E5.sketch_text.stroke-52"),sQuery(id+"F0.wireOp",EDGE,"E5.sketch_text.stroke-53"),sQuery(id+"F0.wireOp",EDGE,"E5.sketch_text.stroke-54"),sQuery(id+"F0.wireOp",EDGE,"E5.sketch_text.stroke-55"),sQuery(id+"F0.wireOp",EDGE,"E5.sketch_text.stroke-56"),sQuery(id+"F0.wireOp",EDGE,"E5.sketch_text.stroke-57"),sQuery(id+"F0.wireOp",EDGE,"E5.sketch_text.stroke-58"),sQuery(id+"F0.wireOp",EDGE,"E5.sketch_text.stroke-59"),sQuery(id+"F0.wireOp",EDGE,"E5.sketch_text.stroke-60"),sQuery(id+"F0.wireOp",EDGE,"E5.sketch_text.stroke-61"),sQuery(id+"F0.wireOp",EDGE,"E5.sketch_text.stroke-62"),sQuery(id+"F0.wireOp",EDGE,"E5.sketch_text.stroke-63"),sQuery(id+"F0.wireOp",EDGE,"E5.sketch_text.stroke-64"),sQuery(id+"F0.wireOp",EDGE,"E5.sketch_text.stroke-65"),sQuery(id+"F0.wireOp",EDGE,"E5.sketch_text.stroke-66"),sQuery(id+"F0.wireOp",EDGE,"E5.sketch_text.stroke-67"),sQuery(id+"F0.wireOp",EDGE,"E5.sketch_text.stroke-68"),sQuery(id+"F0.wireOp",EDGE,"E5.sketch_text.stroke-69"),sQuery(id+"F0.wireOp",EDGE,"E5.sketch_text.stroke-70"),sQuery(id+"F0.wireOp",EDGE,"E5.sketch_text.stroke-71"),sQuery(id+"F0.wireOp",EDGE,"E5.sketch_text.stroke-72"),sQuery(id+"F0.wireOp",EDGE,"E5.sketch_text.stroke-73"),sQuery(id+"F0.wireOp",EDGE,"E5.sketch_text.stroke-74"),sQuery(id+"F0.wireOp",EDGE,"E5.sketch_text.stroke-75"),sQuery(id+"F0.wireOp",EDGE,"E5.sketch_text.stroke-76"),sQuery(id+"F0.wireOp",EDGE,"E5.sketch_text.stroke-77"),sQuery(id+"F0.wireOp",EDGE,"E5.sketch_text.stroke-78"),sQuery(id+"F0.wireOp",EDGE,"E5.sketch_text.stroke-79"),sQuery(id+"F0.wireOp",EDGE,"E5.sketch_text.stroke-80"),sQuery(id+"F0.wireOp",EDGE,"E5.sketch_text.stroke-81"),sQuery(id+"F0.wireOp",EDGE,"E5.sketch_text.stroke-82"),sQuery(id+"F0.wireOp",EDGE,"E5.sketch_text.stroke-83"),sQuery(id+"F0.wireOp",EDGE,"E5.sketch_text.stroke-84"),sQuery(id+"F0.wireOp",EDGE,"E5.sketch_text.stroke-85"),sQuery(id+"F0.wireOp",EDGE,"E5.sketch_text.stroke-86"),sQuery(id+"F0.wireOp",EDGE,"E5.sketch_text.stroke-87"),sQuery(id+"F0.wireOp",EDGE,"E5.sketch_text.stroke-88"),sQuery(id+"F0.wireOp",EDGE,"E5.sketch_text.stroke-89"),sQuery(id+"F0.wireOp",EDGE,"E5.sketch_text.stroke-90"),sQuery(id+"F0.wireOp",EDGE,"E5.sketch_text.stroke-91"),sQuery(id+"F0.wireOp",EDGE,"E5.sketch_text.stroke-92"),sQuery(id+"F0.wireOp",EDGE,"E5.sketch_text.stroke-93"),sQuery(id+"F0.wireOp",EDGE,"E5.sketch_text.stroke-94"),sQuery(id+"F0.wireOp",EDGE,"E5.sketch_text.stroke-95"),sQuery(id+"F0.wireOp",EDGE,"E5.sketch_text.stroke-96"),sQuery(id+"F0.wireOp",EDGE,"E5.sketch_text.stroke-97"),sQuery(id+"F0.wireOp",EDGE,"E5.sketch_text.stroke-98"),sQuery(id+"F0.wireOp",EDGE,"E5.sketch_text.stroke-99"),sQuery(id+"F0.wireOp",EDGE,"E5.sketch_text.stroke-100"),sQuery(id+"F0.wireOp",EDGE,"E5.sketch_text.stroke-101"),sQuery(id+"F0.wireOp",EDGE,"E5.sketch_text.stroke-102"),sQuery(id+"F0.wireOp",EDGE,"E5.sketch_text.stroke-103"),sQuery(id+"F0.wireOp",EDGE,"E5.sketch_text.stroke-104"),sQuery(id+"F0.wireOp",EDGE,"E5.sketch_text.stroke-105"),sQuery(id+"F0.wireOp",EDGE,"E5.sketch_text.stroke-106"),sQuery(id+"F0.wireOp",EDGE,"E5.sketch_text.stroke-107"),sQuery(id+"F0.wireOp",EDGE,"E5.sketch_text.stroke-108"),sQuery(id+"F0.wireOp",EDGE,"E5.sketch_text.stroke-109"),sQuery(id+"F0.wireOp",EDGE,"E5.sketch_text.stroke-110"),sQuery(id+"F0.wireOp",EDGE,"E5.sketch_text.stroke-111"),sQuery(id+"F0.wireOp",EDGE,"E5.sketch_text.stroke-112"),sQuery(id+"F0.wireOp",EDGE,"E5.sketch_text.stroke-113"),sQuery(id+"F0.wireOp",EDGE,"E5.sketch_text.stroke-114"),sQuery(id+"F0.wireOp",EDGE,"E5.sketch_text.stroke-115"),sQuery(id+"F0.wireOp",EDGE,"E5.sketch_text.stroke-116"),sQuery(id+"F0.wireOp",EDGE,"E5.sketch_text.stroke-117"),sQuery(id+"F0.wireOp",EDGE,"E5.sketch_text.stroke-118"),sQuery(id+"F0.wireOp",EDGE,"E5.sketch_text.stroke-119"),sQuery(id+"F0.wireOp",EDGE,"E5.sketch_text.stroke-120"),sQuery(id+"F0.wireOp",EDGE,"E5.sketch_text.stroke-121"),sQuery(id+"F0.wireOp",EDGE,"E5.sketch_text.stroke-122"),sQuery(id+"F0.wireOp",EDGE,"E5.sketch_text.stroke-123"),sQuery(id+"F0.wireOp",EDGE,"E5.sketch_text.stroke-124"),sQuery(id+"F0.wireOp",EDGE,"E5.sketch_text.stroke-125"),sQuery(id+"F0.wireOp",EDGE,"E5.sketch_text.stroke-126"),sQuery(id+"F0.wireOp",EDGE,"E5.sketch_text.stroke-127"),sQuery(id+"F0.wireOp",EDGE,"E5.sketch_text.stroke-128"),sQuery(id+"F0.wireOp",EDGE,"E5.sketch_text.stroke-129"),sQuery(id+"F0.wireOp",EDGE,"E5.sketch_text.stroke-130"),sQuery(id+"F0.wireOp",EDGE,"E5.sketch_text.stroke-131"),sQuery(id+"F0.wireOp",EDGE,"E5.sketch_text.stroke-132"),sQuery(id+"F0.wireOp",EDGE,"E5.sketch_text.stroke-133"),sQuery(id+"F0.wireOp",EDGE,"E5.sketch_text.stroke-134"),sQuery(id+"F0.wireOp",EDGE,"E5.sketch_text.stroke-135"),sQuery(id+"F0.wireOp",EDGE,"E5.sketch_text.stroke-136"),sQuery(id+"F0.wireOp",EDGE,"E5.sketch_text.stroke-137"),sQuery(id+"F0.wireOp",EDGE,"E5.sketch_text.stroke-138"),sQuery(id+"F0.wireOp",EDGE,"E5.sketch_text.stroke-139"),sQuery(id+"F0.wireOp",EDGE,"E5.sketch_text.stroke-140"),sQuery(id+"F0.wireOp",EDGE,"E5.sketch_text.stroke-141"),sQuery(id+"F0.wireOp",EDGE,"E5.sketch_text.stroke-142"),sQuery(id+"F0.wireOp",EDGE,"E6.0"),sQuery(id+"F0.wireOp",EDGE,"E7.0"),sQuery(id+"F0.wireOp",EDGE,"E7.1"),sQuery(id+"F0.wireOp",EDGE,"E8"),sQuery(id+"F0.wireOp",EDGE,"E9.trimOffspring"),sQuery(id+"F0.wireOp",EDGE,"E10")])]});
            deleteBodies(context, id + "F8", {"entities" : qUnion([Q0])});
        }
        {
            var Q0;
            Q0=makeQuery(id+"F0.imprint","IMPRINT",FACE,{"disambiguationData":[TD([[makeQuery(id+"F0.imprint","IMPRINT",EDGE,{"derivedFrom":sQuery(id+"F0.wireOp",EDGE,"E5.sketch_text.stroke-99")}),-1.0]])]});
            var Q1;
            Q1=makeQuery(id+"F0.imprint","IMPRINT",FACE,{"disambiguationData":[TD([[makeQuery(id+"F0.imprint","IMPRINT",EDGE,{"derivedFrom":sQuery(id+"F0.wireOp",EDGE,"E5.sketch_text.stroke-0")}),-1.0]])]});
            var Q2;
            Q2=makeQuery(id+"F0.imprint","IMPRINT",FACE,{"disambiguationData":[TD([[makeQuery(id+"F0.imprint","IMPRINT",EDGE,{"derivedFrom":sQuery(id+"F0.wireOp",EDGE,"E5.sketch_text.stroke-125")}),-1.0]])]});
            var Q3;
            Q3=makeQuery(id+"F0.imprint","IMPRINT",FACE,{"disambiguationData":[TD([[makeQuery(id+"F0.imprint","IMPRINT",EDGE,{"derivedFrom":sQuery(id+"F0.wireOp",EDGE,"E5.sketch_text.stroke-6")}),-1.0]])]});
            var Q4;
            Q4=makeQuery(id+"F0.imprint","IMPRINT",FACE,{"disambiguationData":[TD([[makeQuery(id+"F0.imprint","IMPRINT",EDGE,{"derivedFrom":sQuery(id+"F0.wireOp",EDGE,"E0.bottom")}),-1.0]])]});
            var Q5;
            Q5=makeQuery(id+"F0.imprint","IMPRINT",FACE,{"disambiguationData":[TD([[makeQuery(id+"F0.imprint","IMPRINT",EDGE,{"derivedFrom":sQuery(id+"F0.wireOp",EDGE,"E5.sketch_text.stroke-73")}),-1.0]])]});
            var Q6;
            Q6=makeQuery(id+"F0.imprint","IMPRINT",FACE,{"disambiguationData":[TD([[makeQuery(id+"F0.imprint","IMPRINT",EDGE,{"derivedFrom":sQuery(id+"F0.wireOp",EDGE,"E5.sketch_text.stroke-69")}),-1.0]])]});
            var Q7;
            Q7=makeQuery(id+"F0.imprint","IMPRINT",FACE,{"disambiguationData":[TD([[makeQuery(id+"F0.imprint","IMPRINT",EDGE,{"derivedFrom":sQuery(id+"F0.wireOp",EDGE,"E5.sketch_text.stroke-49")}),-1.0]])]});
            var Q8;
            Q8=makeQuery(id+"F0.imprint","IMPRINT",FACE,{"disambiguationData":[TD([[makeQuery(id+"F0.imprint","IMPRINT",EDGE,{"derivedFrom":sQuery(id+"F0.wireOp",EDGE,"E5.sketch_text.stroke-57")}),-1.0]])]});
            var Q9;
            Q9=makeQuery(id+"F0.imprint","IMPRINT",FACE,{"disambiguationData":[TD([[makeQuery(id+"F0.imprint","IMPRINT",EDGE,{"derivedFrom":sQuery(id+"F0.wireOp",EDGE,"E5.sketch_text.stroke-10")}),-1.0]])]});
            var Q10;
            Q10=makeQuery(id+"F0.imprint","IMPRINT",FACE,{"disambiguationData":[TD([[makeQuery(id+"F0.imprint","IMPRINT",EDGE,{"derivedFrom":sQuery(id+"F0.wireOp",EDGE,"E5.sketch_text.stroke-61")}),-1.0]])]});
            var Q11;
            Q11=makeQuery(id+"F0.imprint","IMPRINT",FACE,{"disambiguationData":[TD([[makeQuery(id+"F0.imprint","IMPRINT",EDGE,{"derivedFrom":sQuery(id+"F0.wireOp",EDGE,"E5.sketch_text.stroke-53")}),-1.0]])]});
            var Q12;
            Q12=makeQuery(id+"F0.imprint","IMPRINT",FACE,{"disambiguationData":[TD([[makeQuery(id+"F0.imprint","IMPRINT",EDGE,{"derivedFrom":sQuery(id+"F0.wireOp",EDGE,"E5.sketch_text.stroke-65")}),-1.0]])]});
            var Q13;
            Q13=makeQuery(id+"F0.imprint","IMPRINT",FACE,{"disambiguationData":[TD([[makeQuery(id+"F0.imprint","IMPRINT",EDGE,{"derivedFrom":sQuery(id+"F0.wireOp",EDGE,"E5.sketch_text.stroke-107")}),-1.0]])]});
            extrude(context, id + "F9", {"entities" : qUnion([Q0, Q1, Q2, Q3, Q4, Q5, Q6, Q7, Q8, Q9, Q10, Q11, Q12, Q13]), "depth" : .6 * mm, "offsetDistance" : 25 * mm});
        }
    });
